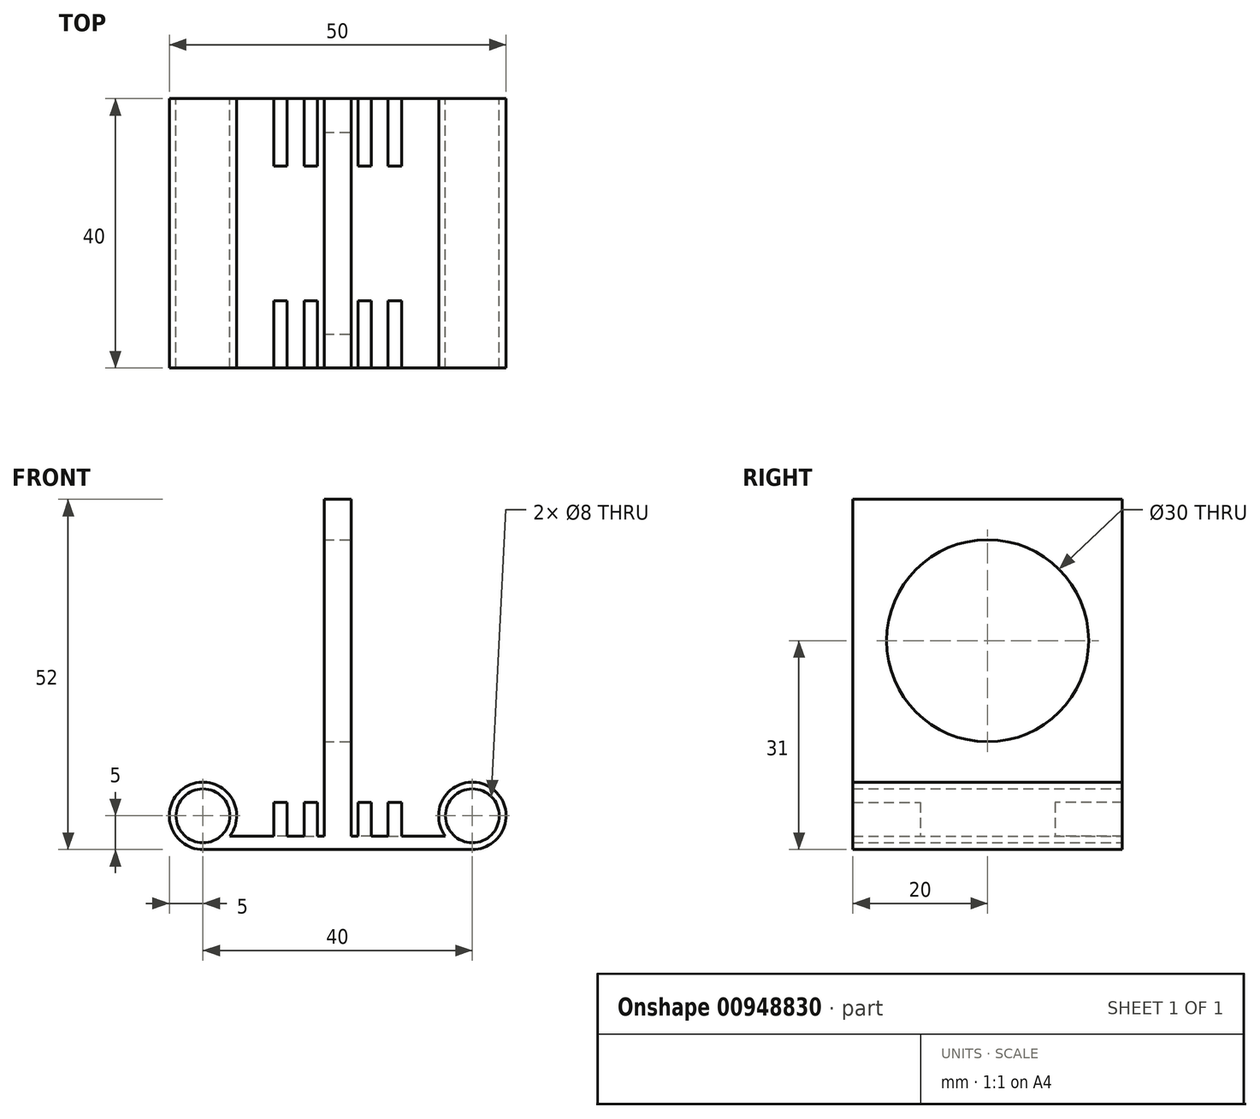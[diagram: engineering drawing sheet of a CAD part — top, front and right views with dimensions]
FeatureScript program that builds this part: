
annotation { "Feature Type Name" : "Feature", "Feature Type Description" : "" }
export const myFeature = defineFeature(function(context is Context, id is Id, definition is map)
    precondition{}
    {
        {
            var Q0;
            Q0=qCreatedBy(makeId("Front.planeOp"),FACE);
            var sketch = newSketch(context, id + "F0", { "sketchPlane" : qUnion([Q0])});
            skLineSegment(sketch, "E0.bottom", {"start": v(20, -1) * mm, "end": v(-20, -1) * mm});
            skLineSegment(sketch, "E0.top", {"start": v(16, 1) * mm, "end": v(-20, 1) * mm});
            skLineSegment(sketch, "E0.right", {"start": v(-20, -1) * mm, "end": v(-20, 1) * mm});
            skPoint(sketch, "E0.middle", {"position": v(0, 0) * mm});
            skArc(sketch, "E1", {"start": v(20, -1) * mm, "mid": v(22.24, 8.47) * mm, "end": v(16, 1) * mm});
            skPoint(sketch, "E1.second.point", {"position": v(20, 9) * mm});
            skPoint(sketch, "E1.third.point", {"position": v(24.89, 5.05) * mm});
            skCircle(sketch, "E2", {"center": v(20, 4) * mm, "radius": 4 * mm});
            skPoint(sketch, "E3.orphan", {"position": v(20, 1) * mm});
            skLineSegment(sketch, "E4.bottom", {"start": v(-2, 1) * mm, "end": v(2, 1) * mm});
            skLineSegment(sketch, "E4.top", {"start": v(-2, 51) * mm, "end": v(2, 51) * mm});
            skLineSegment(sketch, "E4.left", {"start": v(-2, 1) * mm, "end": v(-2, 51) * mm});
            skLineSegment(sketch, "E4.right", {"start": v(2, 1) * mm, "end": v(2, 51) * mm});
            skArc(sketch, "E5.MirrorCS", {"start": v(-20, -1) * mm, "mid": v(-22.24, 8.47) * mm, "end": v(-16, 1) * mm});
            skCircle(sketch, "E6.MirrorC", {"center": v(-20, 4) * mm, "radius": 4 * mm});
            skPoint(sketch, "E7.MirrorP", {"position": v(-20, 9) * mm});
            skPoint(sketch, "E8.MirrorP", {"position": v(-24.89, 5.05) * mm});
            skPoint(sketch, "E9.MirrorP", {"position": v(-20, 1) * mm});
            skSolve(sketch);
        }
        {
            var Q0;
            Q0=qSketchRegion(id+"F0",true);
            extrude(context, id + "F1", {"entities" : qUnion([Q0]), "endBound" : BoundingType.SYMMETRIC, "depth" : 40 * mm, "offsetDistance" : 25 * mm});
        }
        {
            var Q0;
            {var subQ0=sQuery(id+"F0.wireOp",EDGE,"E0.top");Q0=makeQuery(id+"F1.opExtrude","SWEPT_FACE",FACE,{"disambiguationData":[OSD([subQ0]),TDD([makeQuery(id+"F0.imprint","IMPRINT",EDGE,{"disambiguationData":[TD([[makeQuery(id+"F0.imprint","INTERSECT",VERTEX,{"derivedFrom":[subQ0,sQuery(id+"F0.wireOp",EDGE,"E1")]}),-1.0]])],"derivedFrom":subQ0})])]});}
            var sketch = newSketch(context, id + "F2", { "sketchPlane" : qUnion([Q0])});
            skLineSegment(sketch, "E10.bottom", {"start": v(7.5, -20) * mm, "end": v(9.5, -20) * mm});
            skLineSegment(sketch, "E10.top", {"start": v(7.5, -10) * mm, "end": v(9.5, -10) * mm});
            skLineSegment(sketch, "E10.left", {"start": v(7.5, -20) * mm, "end": v(7.5, -10) * mm});
            skLineSegment(sketch, "E10.right", {"start": v(9.5, -20) * mm, "end": v(9.5, -10) * mm});
            skLineSegment(sketch, "E11.bottom", {"start": v(5, -20) * mm, "end": v(3, -20) * mm});
            skLineSegment(sketch, "E11.top", {"start": v(5, -10) * mm, "end": v(3, -10) * mm});
            skLineSegment(sketch, "E11.left", {"start": v(5, -20) * mm, "end": v(5, -10) * mm});
            skLineSegment(sketch, "E11.right", {"start": v(3, -20) * mm, "end": v(3, -10) * mm});
            skLineSegment(sketch, "E12.MirrorCS", {"start": v(-7.5, -20) * mm, "end": v(-7.5, -10) * mm});
            skLineSegment(sketch, "E13.MirrorCS", {"start": v(-5, -20) * mm, "end": v(-3, -20) * mm});
            skLineSegment(sketch, "E14.MirrorCS", {"start": v(-5, -20) * mm, "end": v(-5, -10) * mm});
            skLineSegment(sketch, "E15.MirrorCS", {"start": v(-3, -20) * mm, "end": v(-3, -10) * mm});
            skLineSegment(sketch, "E16.MirrorCS", {"start": v(-7.5, -20) * mm, "end": v(-9.5, -20) * mm});
            skLineSegment(sketch, "E17.MirrorCS", {"start": v(-9.5, -20) * mm, "end": v(-9.5, -10) * mm});
            skLineSegment(sketch, "E18.MirrorCS", {"start": v(-5, -10) * mm, "end": v(-3, -10) * mm});
            skLineSegment(sketch, "E19.MirrorCS", {"start": v(-7.5, -10) * mm, "end": v(-9.5, -10) * mm});
            skLineSegment(sketch, "E20.MirrorCS", {"start": v(7.5, 10) * mm, "end": v(9.5, 10) * mm});
            skLineSegment(sketch, "E21.MirrorCS", {"start": v(-7.5, 10) * mm, "end": v(-9.5, 10) * mm});
            skLineSegment(sketch, "E22.MirrorCS", {"start": v(7.5, 20) * mm, "end": v(9.5, 20) * mm});
            skLineSegment(sketch, "E23.MirrorCS", {"start": v(-5, 10) * mm, "end": v(-3, 10) * mm});
            skLineSegment(sketch, "E24.MirrorCS", {"start": v(5, 20) * mm, "end": v(3, 20) * mm});
            skLineSegment(sketch, "E25.MirrorCS", {"start": v(-7.5, 20) * mm, "end": v(-9.5, 20) * mm});
            skLineSegment(sketch, "E26.MirrorCS", {"start": v(-5, 20) * mm, "end": v(-3, 20) * mm});
            skLineSegment(sketch, "E27.MirrorCS", {"start": v(5, 10) * mm, "end": v(3, 10) * mm});
            skLineSegment(sketch, "E28.MirrorCS", {"start": v(-7.5, 20) * mm, "end": v(-7.5, 10) * mm});
            skLineSegment(sketch, "E29.MirrorCS", {"start": v(3, 20) * mm, "end": v(3, 10) * mm});
            skLineSegment(sketch, "E30.MirrorCS", {"start": v(-9.5, 20) * mm, "end": v(-9.5, 10) * mm});
            skLineSegment(sketch, "E31.MirrorCS", {"start": v(5, 20) * mm, "end": v(5, 10) * mm});
            skLineSegment(sketch, "E32.MirrorCS", {"start": v(9.5, 20) * mm, "end": v(9.5, 10) * mm});
            skLineSegment(sketch, "E33.MirrorCS", {"start": v(-3, 20) * mm, "end": v(-3, 10) * mm});
            skLineSegment(sketch, "E34.MirrorCS", {"start": v(-5, 20) * mm, "end": v(-5, 10) * mm});
            skLineSegment(sketch, "E35.MirrorCS", {"start": v(7.5, 20) * mm, "end": v(7.5, 10) * mm});
            skSolve(sketch);
        }
        {
            var Q0;
            Q0=qSketchRegion(id+"F2",true);
            extrude(context, id + "F3", {"entities" : qUnion([Q0]), "operationType" : NewBodyOperationType.ADD, "depth" : 5 * mm, "offsetDistance" : 25 * mm});
        }
        {
            var Q0;
            Q0=makeQuery(id+"F1.opExtrude","SWEPT_FACE",FACE,{"disambiguationData":[OSD([sQuery(id+"F0.wireOp",EDGE,"E4.right")])]});
            var sketch = newSketch(context, id + "F4", { "sketchPlane" : qUnion([Q0])});
            skCircle(sketch, "E36", {"center": v(0, 30) * mm, "radius": 15 * mm});
            skSolve(sketch);
        }
        {
            var Q0;
            Q0=qSketchRegion(id+"F4",true);
            extrude(context, id + "F5", {"entities" : qUnion([Q0]), "operationType" : NewBodyOperationType.REMOVE, "oppositeDirection" : true, "depth" : 25 * mm, "offsetDistance" : 25 * mm});
        }
        {
            var Q0;
            Q0=qSketchRegion(id+"F2",true);
            extrude(context, id + "F6", {"entities" : qUnion([Q0]), "operationType" : NewBodyOperationType.ADD, "depth" : 5 * mm, "offsetDistance" : 25 * mm});
        }
    });
